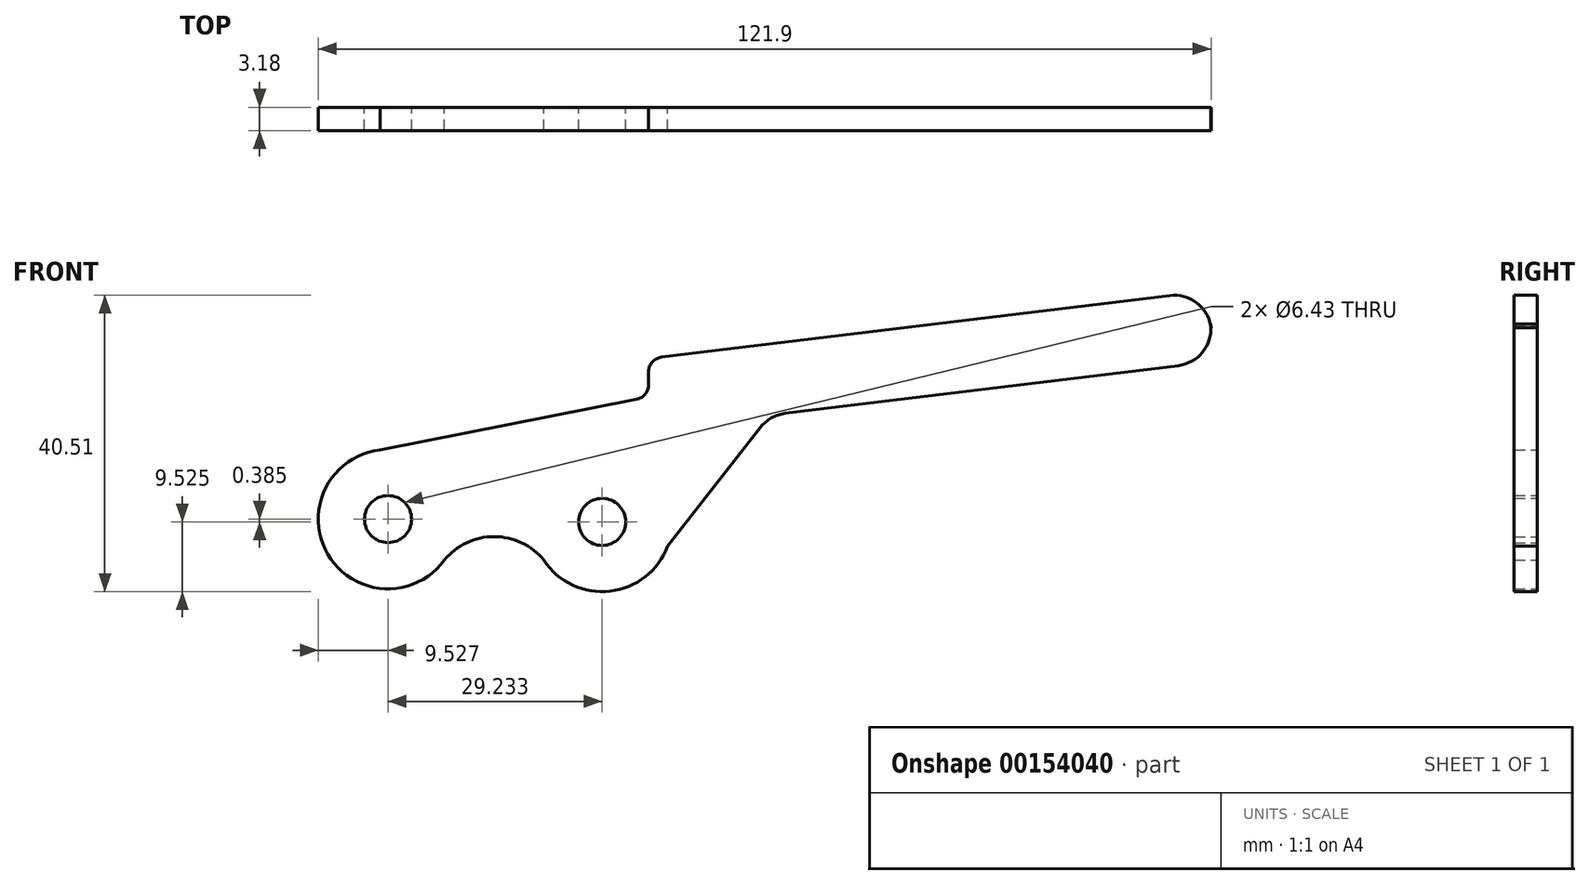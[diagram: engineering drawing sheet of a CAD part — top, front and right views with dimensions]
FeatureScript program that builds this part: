
annotation { "Feature Type Name" : "Feature", "Feature Type Description" : "" }
export const myFeature = defineFeature(function(context is Context, id is Id, definition is map)
    precondition{}
    {
        {
            var Q0;
            Q0=qCreatedBy(makeId("Front.planeOp"),FACE);
            var sketch = newSketch(context, id + "F0", { "sketchPlane" : qUnion([Q0])});
            skCircle(sketch, "E0", {"center": v(-11.03, 11.14) * mm, "radius": 3.21 * mm});
            skCircle(sketch, "E1", {"center": v(18.2, 10.75) * mm, "radius": 3.21 * mm});
            skArc(sketch, "E2", {"start": v(-12.12, 20.6) * mm, "mid": v(-19.26, 6.34) * mm, "end": v(-3.33, 5.54) * mm});
            skArc(sketch, "E3", {"start": v(10.24, 5.53) * mm, "mid": v(19.26, 1.29) * mm, "end": v(27.12, 7.42) * mm});
            skLineSegment(sketch, "E4", {"start": v(-12.12, 20.6) * mm, "end": v(22.9, 27.5) * mm});
            skLineSegment(sketch, "E5", {"start": v(24.53, 29.5) * mm, "end": v(24.53, 31.25) * mm});
            skLineSegment(sketch, "E6", {"start": v(26.32, 33.27) * mm, "end": v(95.69, 41.7) * mm});
            skLineSegment(sketch, "E7.0", {"start": v(43.2, 25.6) * mm, "end": v(96.85, 32.12) * mm});
            skLineSegment(sketch, "E8", {"start": v(101.28, 37.78) * mm, "end": v(101.34, 37.27) * mm});
            skLineSegment(sketch, "E9", {"start": v(39.81, 23.68) * mm, "end": v(27.12, 7.42) * mm});
            skArc(sketch, "E10", {"start": v(10.24, 5.53) * mm, "mid": v(3.46, 8.75) * mm, "end": v(-3.33, 5.54) * mm});
            skPoint(sketch, "E11.visualSharp", {"position": v(24.53, 33.05) * mm});
            skArc(sketch, "E11.filletArc", {"start": v(26.32, 33.27) * mm, "mid": v(25.04, 32.6) * mm, "end": v(24.53, 31.25) * mm});
            skPoint(sketch, "E12.visualSharp", {"position": v(24.53, 27.83) * mm});
            skArc(sketch, "E12.filletArc", {"start": v(22.9, 27.5) * mm, "mid": v(24.07, 28.2) * mm, "end": v(24.53, 29.5) * mm});
            skPoint(sketch, "E13.visualSharp", {"position": v(100.73, 42.31) * mm});
            skArc(sketch, "E13.filletArc", {"start": v(101.34, 37.27) * mm, "mid": v(99.43, 40.66) * mm, "end": v(95.69, 41.7) * mm});
            skPoint(sketch, "E14.visualSharp", {"position": v(101.9, 32.73) * mm});
            skArc(sketch, "E14.filletArc", {"start": v(96.85, 32.12) * mm, "mid": v(100.24, 34.03) * mm, "end": v(101.28, 37.78) * mm});
            skPoint(sketch, "E15.visualSharp", {"position": v(41.1, 25.34) * mm});
            skArc(sketch, "E15.filletArc", {"start": v(43.2, 25.6) * mm, "mid": v(41.32, 24.98) * mm, "end": v(39.81, 23.68) * mm});
            skSolve(sketch);
        }
        {
            var Q0;
            Q0 = qSketchRegion(id + "F0", true);
            extrude(context, id + "F1", {"entities" : qUnion([Q0]), "depth" : 3.17 * mm});
        }
    });
